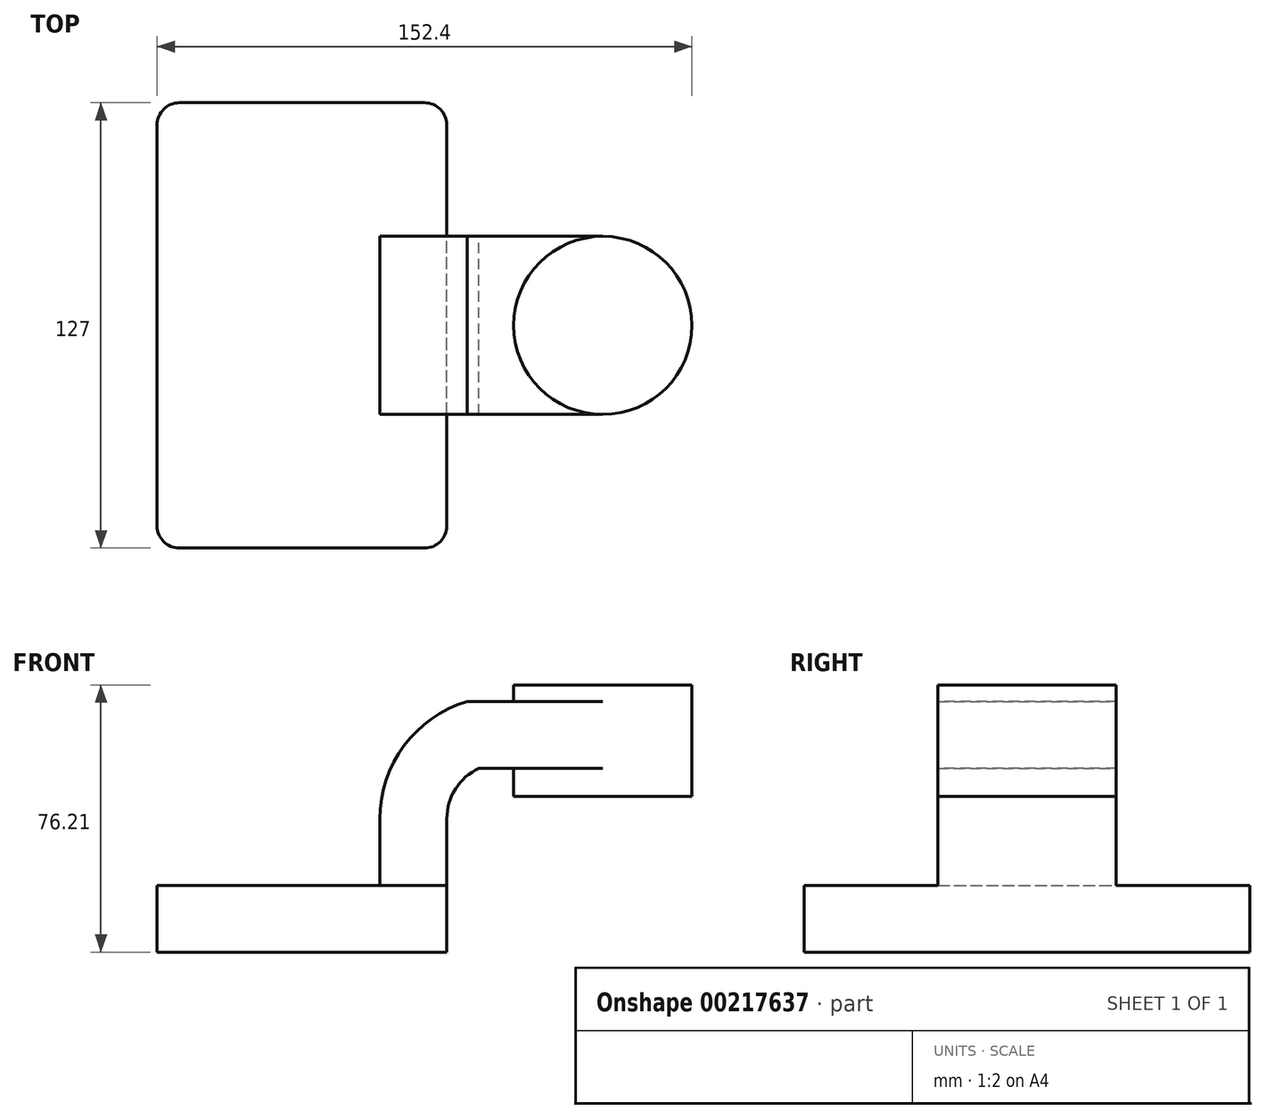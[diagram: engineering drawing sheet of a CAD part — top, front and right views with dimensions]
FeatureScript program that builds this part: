
annotation { "Feature Type Name" : "Feature", "Feature Type Description" : "" }
export const myFeature = defineFeature(function(context is Context, id is Id, definition is map)
    precondition{}
    {
        {
            var Q0;
            Q0=qCreatedBy(makeId("Front.planeOp"),FACE);
            var sketch = newSketch(context, id + "F0", { "sketchPlane" : qUnion([Q0])});
            skLineSegment(sketch, "E0.bottom", {"start": v(41.27, 9.53) * mm, "end": v(-41.28, 9.53) * mm});
            skLineSegment(sketch, "E0.top", {"start": v(41.28, -9.52) * mm, "end": v(-41.27, -9.52) * mm});
            skLineSegment(sketch, "E0.left", {"start": v(41.28, 9.53) * mm, "end": v(41.28, -9.52) * mm});
            skLineSegment(sketch, "E0.right", {"start": v(-41.28, 9.53) * mm, "end": v(-41.27, -9.52) * mm});
            skPoint(sketch, "E0.middle", {"position": v(0, 0) * mm});
            skLineSegment(sketch, "E1.bottom", {"start": v(60.32, 66.68) * mm, "end": v(111.12, 66.68) * mm});
            skLineSegment(sketch, "E1.top", {"start": v(60.33, 34.92) * mm, "end": v(111.12, 34.93) * mm});
            skLineSegment(sketch, "E1.left", {"start": v(60.33, 66.68) * mm, "end": v(60.33, 34.93) * mm});
            skLineSegment(sketch, "E1.right", {"start": v(111.13, 66.68) * mm, "end": v(111.13, 34.93) * mm});
            skLineSegment(sketch, "E2", {"start": v(41.27, 9.53) * mm, "end": v(41.27, 28.5) * mm});
            skArc(sketch, "E3", {"start": v(41.27, 28.5) * mm, "mid": v(43.76, 37.02) * mm, "end": v(50.42, 42.88) * mm});
            skLineSegment(sketch, "E4", {"start": v(50.42, 42.88) * mm, "end": v(85.72, 42.88) * mm});
            skPoint(sketch, "E4.endSnap0", {"position": v(85.72, 34.93) * mm});
            skPoint(sketch, "E5", {"position": v(85.72, 50.8) * mm});
            skPoint(sketch, "E5.positionSnap0", {"position": v(60.33, 50.8) * mm});
            skPoint(sketch, "E5.positionSnap1", {"position": v(85.72, 66.68) * mm});
            skLineSegment(sketch, "E6.0", {"start": v(47.04, 61.93) * mm, "end": v(85.73, 61.93) * mm});
            skArc(sketch, "E6.1", {"start": v(22.23, 28.5) * mm, "mid": v(29.1, 49.31) * mm, "end": v(47.04, 61.93) * mm});
            skLineSegment(sketch, "E6.2", {"start": v(22.23, 9.53) * mm, "end": v(22.23, 28.5) * mm});
            skLineSegment(sketch, "E7", {"start": v(85.72, 66.68) * mm, "end": v(85.72, 34.93) * mm});
            skFitSpline(sketch, "E8", {"points": [v(-41.28, 9.53) * mm, v(47.04, 61.93) * mm], "startDerivative": vector(4.2, 95.7) * mm, "endDerivative": vector(124.44, -0.9) * mm});
            skSolve(sketch);
        }
        {
            var Q0;
            Q0=makeQuery(id+"F0.imprint","IMPRINT",FACE,{"disambiguationData":[TD([[makeQuery(id+"F0.imprint","IMPRINT",EDGE,{"derivedFrom":sQuery(id+"F0.wireOp",EDGE,"E0.top")}),-1.0]])]});
            extrude(context, id + "F1", {"entities" : qUnion([Q0]), "endBound" : BoundingType.SYMMETRIC, "depth" : 127 * mm});
        }
        {
            var Q0;
            {var subQ1=sQuery(id+"F0.wireOp",EDGE,"E2");Q0=makeQuery(id+"F0.imprint","IMPRINT",FACE,{"disambiguationData":[TD([[makeQuery(id+"F0.imprint","IMPRINT",EDGE,{"derivedFrom":subQ1}),1.0]])]});}
            var Q1;
            {var subQ0=sQuery(id+"F0.wireOp",EDGE,"E6.0");var subQ1=sQuery(id+"F0.wireOp",EDGE,"E1.left");var subQ2=makeQuery(id+"F0.imprint","INTERSECT",VERTEX,{"derivedFrom":[subQ1,subQ0]});Q1=makeQuery(id+"F0.imprint","IMPRINT",FACE,{"disambiguationData":[TD([[makeQuery(id+"F0.imprint","IMPRINT",EDGE,{"disambiguationData":[TD([[subQ2,-1.0]])],"derivedFrom":subQ1}),1.0]])]});}
            extrude(context, id + "F2", {"entities" : qUnion([Q0, Q1]), "operationType" : NewBodyOperationType.ADD, "endBound" : BoundingType.SYMMETRIC, "depth" : 50.8 * mm});
        }
        {
            var Q0;
            Q0=makeQuery(id+"F0.imprint","IMPRINT",FACE,{"disambiguationData":[TD([[makeQuery(id+"F0.imprint","IMPRINT",EDGE,{"derivedFrom":sQuery(id+"F0.wireOp",EDGE,"E6.1")}),1.0]])]});
            extrude(context, id + "F3", {"entities" : qUnion([Q0]), "operationType" : NewBodyOperationType.ADD, "endBound" : BoundingType.SYMMETRIC, "depth" : 15.88 * mm});
        }
        {
            var Q0;
            {var subQ0=sQuery(id+"F0.wireOp",EDGE,"E1.right");Q0=makeQuery(id+"F0.imprint","IMPRINT",FACE,{"disambiguationData":[TD([[makeQuery(id+"F0.imprint","IMPRINT",EDGE,{"derivedFrom":subQ0}),-1.0]])]});}
            var Q1;
            Q1=sQuery(id+"F0.wireOp",EDGE,"E7");
            revolve(context, id + "F4", {"operationType" : NewBodyOperationType.ADD, "entities" : qUnion([Q0]), "axis" : qUnion([Q1]), "revolveType" : RevolveType.FULL});
        }
        {
            var Q0;
            Q0=makeQuery(id+"F1.opExtrude","CAP_EDGE",EDGE,{"disambiguationData":[OSD([sQuery(id+"F0.wireOp",EDGE,"E0.right")])],"isStart":false});
            var Q1;
            Q1=makeQuery(id+"F1.opExtrude","CAP_EDGE",EDGE,{"disambiguationData":[OSD([sQuery(id+"F0.wireOp",EDGE,"E0.left")])],"isStart":false});
            var Q2;
            Q2=makeQuery(id+"F1.opExtrude","CAP_EDGE",EDGE,{"disambiguationData":[OSD([sQuery(id+"F0.wireOp",EDGE,"E0.left")])],"isStart":true});
            var Q3;
            Q3=makeQuery(id+"F1.opExtrude","CAP_EDGE",EDGE,{"disambiguationData":[OSD([sQuery(id+"F0.wireOp",EDGE,"E0.right")])],"isStart":true});
            fillet(context, id + "F5", {"entities" : qUnion([Q0, Q1, Q2, Q3]), "radius" : 6.35 * mm, "tangentPropagation" : true, "allowEdgeOverflow" : false});
        }
    });
